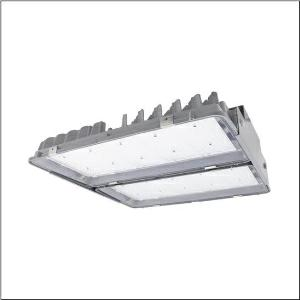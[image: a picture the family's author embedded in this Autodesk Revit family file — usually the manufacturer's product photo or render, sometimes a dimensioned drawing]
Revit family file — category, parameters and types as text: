
# Revit family: highbay_11xtreme_51hf61db4tma
name_source: partatom
category: Lighting Fixtures
units: mm (PartAtom-declared; Revit-internal decimal feet)

## family parameters
Cut with Voids When Loaded = No
Host = Face
Light Source = No
Part Type = Normal
Room Calculation Point = No
Round Connector Dimension = Use Diameter
Shared = No

## types (1)
- --- (1 x LED, 54000 lm, 282.6 W, 4000K)
    Apparent Load = 283 VA
    CIE Flux Codes = 88 96 99 100 100
    Color Rendering = 80
    Color Temperature = 4000K
    Default Elevation = 1800 mm
    Description = Highbay 11Xtreme, LED high bay luminaire, primary light control with lens, of PMMA, primary optical cover: cover, of toughened safety glass, light emission: direct distribution, primary light characteristic: symmetric, installation type: suspended mounting, surface-mounted, 2x LED module,for 1x 2x LED, rated luminous flux: 54.000lm, luminous efficacy: 191lm/W, light colour: 840, colour temperature: 4000K, with cable H07RN-F 5x 1.5mm², mains connection: 220..240V, AC, 50/60Hz, cable length: 1,5m, rated input power: 283W, luminaire housing, of diecast aluminium, coated, silver, length: 595mm, width: 560mm, height: 195mm, protection rating (complete): IP66, insulation class (complete): insulation class I (protective earthing), certification: CE, ENEC, UKCA, protection symbol: D, ball protection: ball impact resistant according to DIN VDE 0710 part 13 (with chain suspension), impact resistance: IK08, permissible operating ambient temperature: -25..+60°C, reducing of maximum allowable ambient temperature of 5°C with ceiling mounting, packaging unit: 1 piece
    Height = 157 mm
    Lamp = 1 x LED
    Lamp Light Flux = 54000 lm
    Lamp Power = 282.6 W
    Lamp count = 1
    Length = 593 mm
    Luminous efficacy = 191 lm/W
    Manufacturer = Siteco
    ModVariant = No
    Model = 51HF61DB4TMA
    Mounting Place = Ceiling
    Mounting Type = Pendant
    Number of Poles = 1
    OnlyDefault = Yes
    Power Factor = 1
    Product Name = Highbay 11Xtreme
    Product group = LED high bay luminaire
    ProductGroupID = 903
    Protection Class = Protection class I
    Protection Degree = IP 66
    RLX_Detail_Level = 1
    RLX_Emergency_Light_Flux = 0 lm
    RLX_Emergency_Type = 0
    RLX_Emergency_Type_DB = No
    RlxData = <blob elided: 33813 chars, md5=85019766>
    Socket = socket
    Standby Power = 0 W
    System Light Flux = 53999 lm
    System Power = 283 W
    Type Comments = factory setting: luminous flux: 100 % | dim-lin: 254 | 960 mA
    Type Image = l_1258340.jpg
    URL = http://relux.com
    VarID = @adj_035797
    Voltage = 0 V
    Weight = 0.00 kg
    Width = 278 mm

## geometry (parser evidence)
native form markers: Blend x4, Sweep x10
no freeform markers — native parametric forms only
